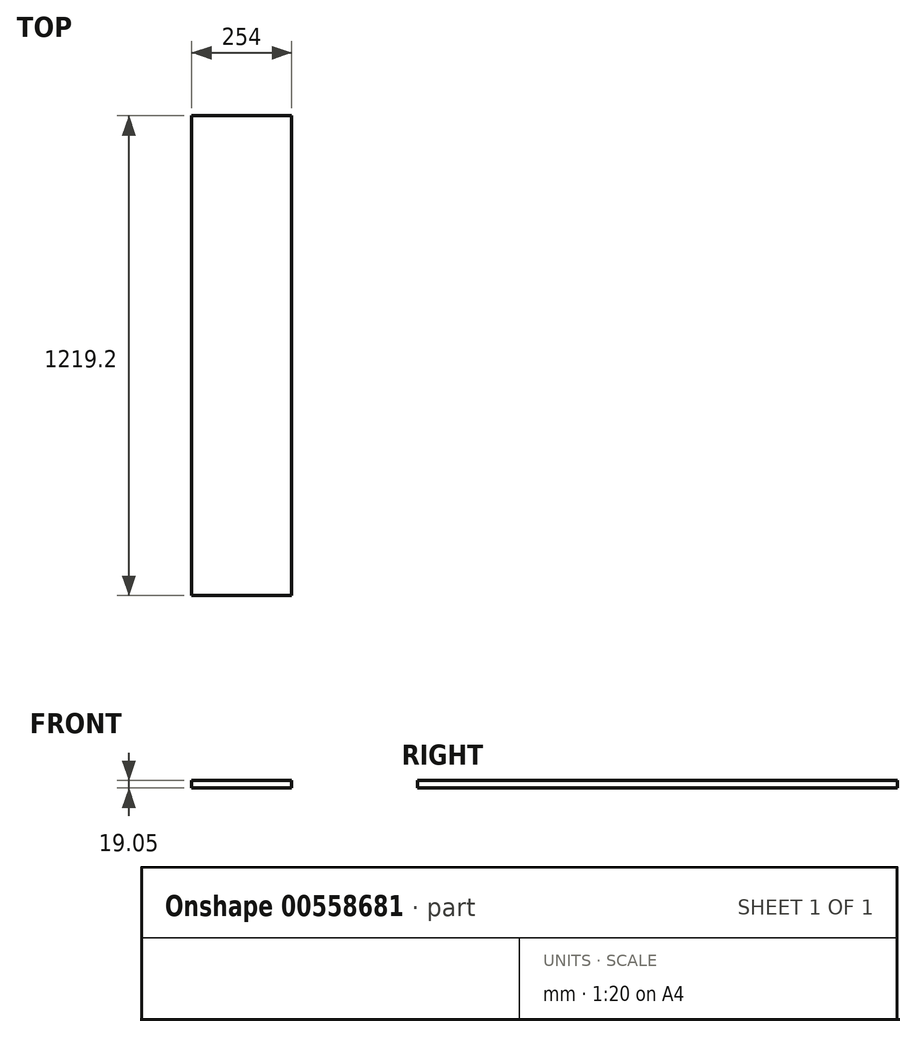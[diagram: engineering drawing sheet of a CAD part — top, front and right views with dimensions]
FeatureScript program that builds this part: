
annotation { "Feature Type Name" : "Feature", "Feature Type Description" : "" }
export const myFeature = defineFeature(function(context is Context, id is Id, definition is map)
    precondition{}
    {
        {
            var Q0;
            Q0=qCreatedBy(makeId("Top.planeOp"),FACE);
            var sketch = newSketch(context, id + "F0", { "sketchPlane" : qUnion([Q0])});
            skLineSegment(sketch, "E0.bottom", {"start": v(284.13, 28.01) * mm, "end": v(30.13, 28.01) * mm});
            skLineSegment(sketch, "E0.top", {"start": v(284.13, 1247.21) * mm, "end": v(30.13, 1247.21) * mm});
            skLineSegment(sketch, "E0.left", {"start": v(284.13, 28.01) * mm, "end": v(284.13, 1247.21) * mm});
            skLineSegment(sketch, "E0.right", {"start": v(30.13, 28.01) * mm, "end": v(30.13, 1247.21) * mm});
            skSolve(sketch);
        }
        {
            var Q0;
            Q0 = qSketchRegion(id + "F0", true);
            extrude(context, id + "F1", {"entities" : qUnion([Q0]), "depth" : 19.05 * mm, "offsetDistance" : 25.4 * mm});
        }
    });
